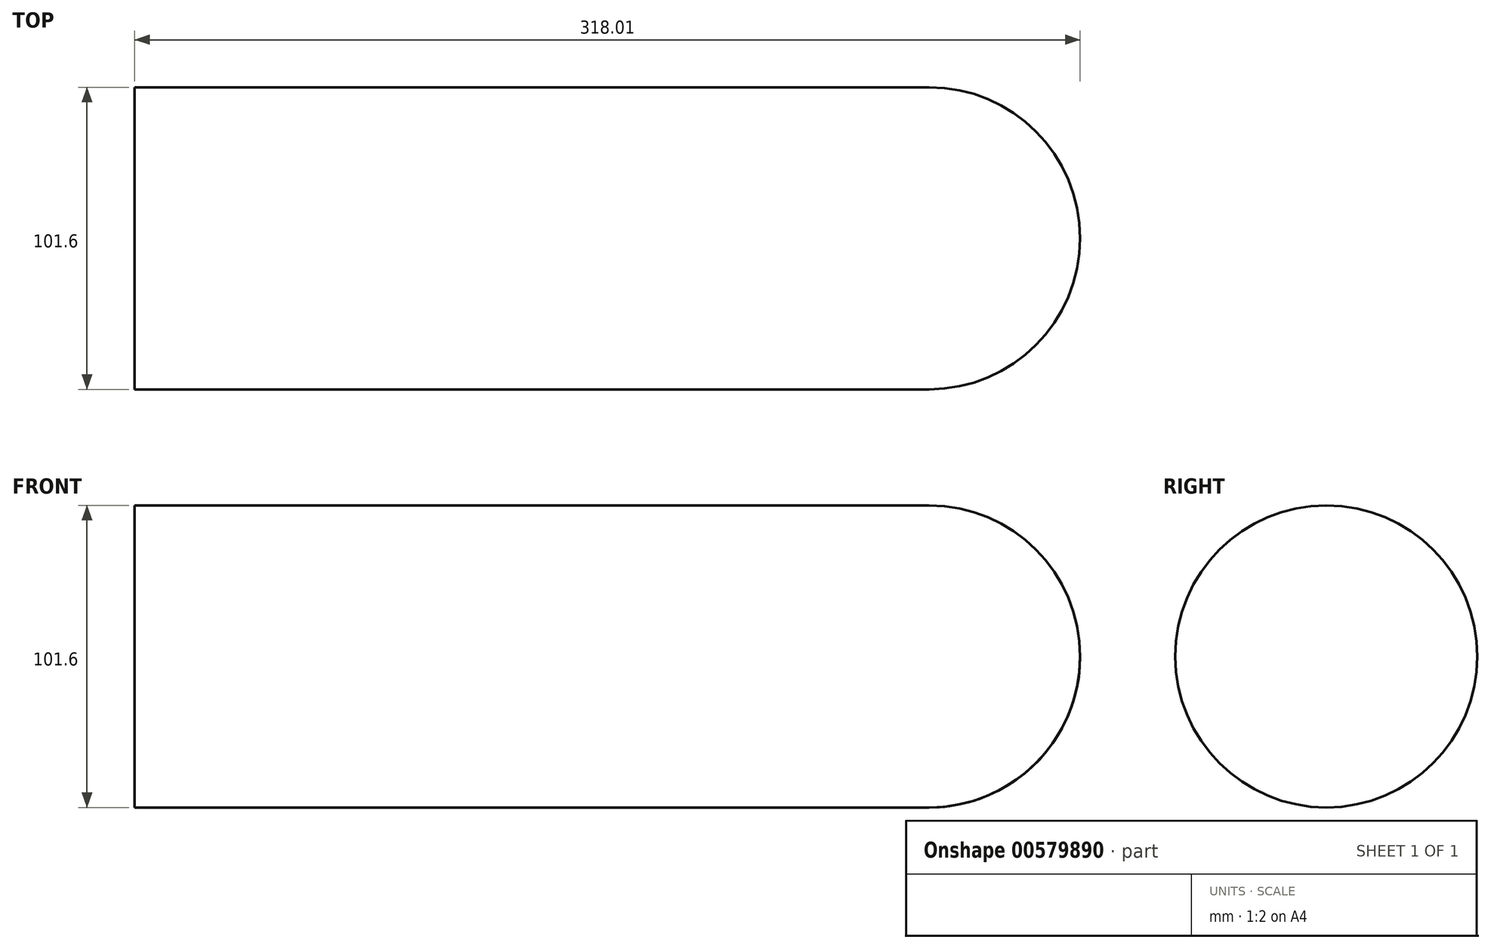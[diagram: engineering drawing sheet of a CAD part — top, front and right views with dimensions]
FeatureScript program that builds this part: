
annotation { "Feature Type Name" : "Feature", "Feature Type Description" : "" }
export const myFeature = defineFeature(function(context is Context, id is Id, definition is map)
    precondition{}
    {
        {
            var Q0;
            Q0=qCreatedBy(makeId("Front.planeOp"),FACE);
            var sketch = newSketch(context, id + "F0", { "sketchPlane" : qUnion([Q0])});
            skCircle(sketch, "E0", {"center": v(0, 0) * mm, "radius": 50.8 * mm});
            skLineSegment(sketch, "E1", {"start": v(0, 50.8) * mm, "end": v(0, -50.8) * mm});
            skLineSegment(sketch, "E2", {"start": v(0, 0) * mm, "end": v(50.8, 0) * mm});
            skSolve(sketch);
        }
        {
            var Q0;
            {var subQ3=sQuery(id+"F0.wireOp",EDGE,"E2");Q0=makeQuery(id+"F0.imprint","IMPRINT",FACE,{"disambiguationData":[TD([[makeQuery(id+"F0.imprint","IMPRINT",EDGE,{"derivedFrom":subQ3}),-1.0]])]});}
            var Q1;
            Q1=sQuery(id+"F0.wireOp",EDGE,"E2");
            revolve(context, id + "F1", {"entities" : qUnion([Q0]), "axis" : qUnion([Q1]), "revolveType" : RevolveType.FULL});
        }
        {
            var Q0;
            Q0=makeQuery(id+"F1.opRevolve","SWEPT_FACE",FACE,{"disambiguationData":[OSD([sQuery(id+"F0.wireOp",EDGE,"E1")])]});
            extrude(context, id + "F2", {"entities" : qUnion([Q0]), "operationType" : NewBodyOperationType.ADD, "depth" : 267.2 * mm, "offsetDistance" : 25.4 * mm});
        }
    });
